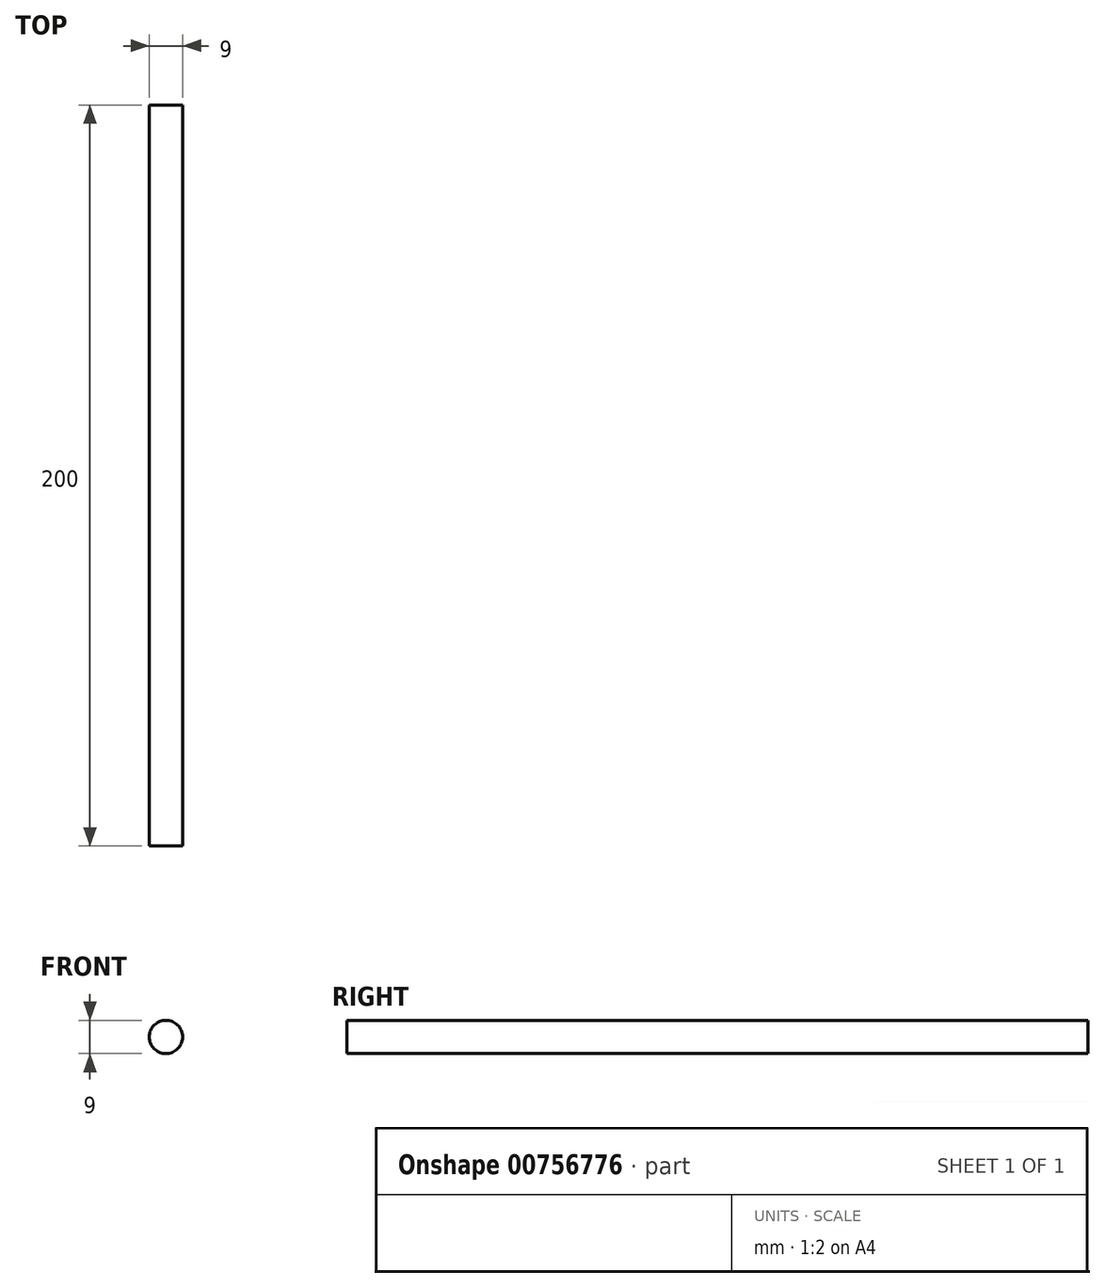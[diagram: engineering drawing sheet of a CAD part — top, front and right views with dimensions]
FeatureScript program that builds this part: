
annotation { "Feature Type Name" : "Feature", "Feature Type Description" : "" }
export const myFeature = defineFeature(function(context is Context, id is Id, definition is map)
    precondition{}
    {
        {
            var Q0;
            Q0=qCreatedBy(makeId("Front.planeOp"),FACE);
            var sketch = newSketch(context, id + "F0", { "sketchPlane" : qUnion([Q0])});
            skCircle(sketch, "E0", {"center": v(0, 0) * mm, "radius": 4.5 * mm});
            skSolve(sketch);
        }
        {
            var Q0;
            Q0=makeQuery(id+"F0.imprint","IMPRINT",FACE,{"disambiguationData":[TD([[makeQuery(id+"F0.imprint","IMPRINT",EDGE,{"derivedFrom":sQuery(id+"F0.wireOp",EDGE,"E0")}),1.0]])]});
            extrude(context, id + "F1", {"entities" : qUnion([Q0]), "depth" : 100 * mm, "offsetDistance" : 25 * mm, "hasSecondDirection" : true, "secondDirectionOppositeDirection" : true, "secondDirectionDepth" : 100 * mm});
        }
    });
